# Revit family: BuroSeating_Konfurb Orbit MB_5 Star
name_source: partatom
category: Furniture
units: mm (PartAtom-declared; Revit-internal decimal feet)

## family parameters
Always vertical = Yes
Cut with Voids When Loaded = No
OmniClass Number = 23.40.70.14.64.11
OmniClass Title = Office Furniture
Room Calculation Point = No
Shared = Yes
Work Plane-Based = No

## types (2) — shared parameters
Assembly Code = E2020
CastorMaterial = BuroSeating_Aluminium_Black
Description = Konfurb Orbit 5 Star Swivel Mid Back
Manufacturer = Buro Seating
Model = KON188
NominalChairHeight = 810-910h
NominalDepth = 600 mm
NominalSeatHeight = 420-520h
NominalWidth = 650 mm  [stored 2.13255 ft]
ProductGroup = Orbit
ProductPageURL AU = https://buroseating.com
ProductPageURL NZ = https://buroseating.co.nz
ProductRange = Buro
SeatArms = No
SeatDepth = 470 mm  [stored 1.54199 ft]
SeatHeadRest = No
SeatLeverHandleMaterial = BuroSeating_Aluminium_Black
SeatTiltMaterial = BuroSeating_Aluminium_Black
SeatWidth = 515 mm  [stored 1.68963 ft]
Type Comments = Seat Height 420-520mm High
URL = https://buroseating.co.nz
URL AU = https://buroseating.com
WarrantyDescription = Full 5 year guarantee (excluding upholstery)
zero-valued in all types: Default Elevation

## per-type parameters (varying)
| type | BaseMaterial | BottomLiftMaterial | CastorWheelMaterial | TopLiftMaterial |
| Buro Elan 159-M3 | BuroSeating_Aluminium_Brushed_Black | BuroSeating_Plastic_Black | BuroSeating_Aluminium_Black | BuroSeating_Aluminium_Black |
| Konfurb Orbit 5 Star Swivel Mid Back | BuroSeating_Aluminium_Black | BuroSeating_Aluminium_Black | BuroSeating_Plastic_Black | BuroSeating_Metal_Chrome_Semi-Polished |

note: [stored X ft] marks values corroborated as IEEE doubles in the binary element streams (Revit-internal decimal feet)

## geometry (parser evidence)
native form markers: Sweep x8
no freeform markers — native parametric forms only
